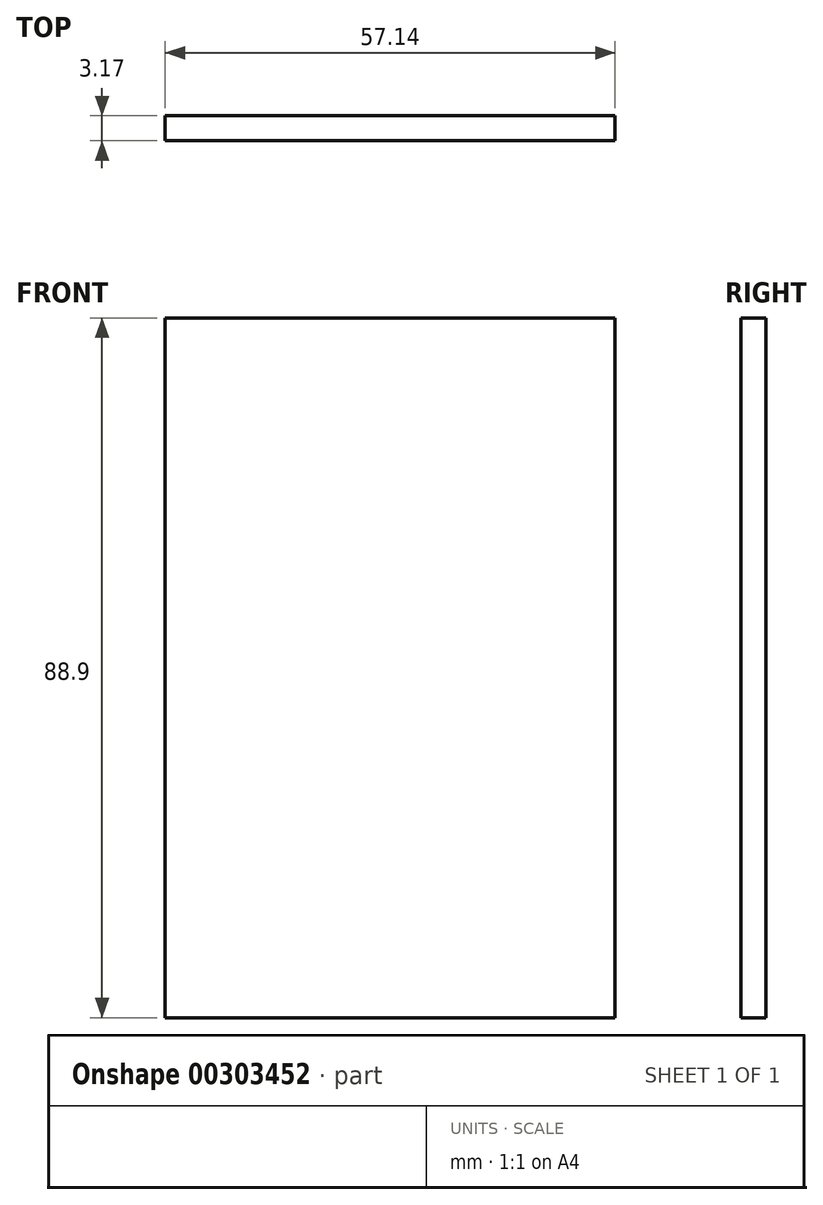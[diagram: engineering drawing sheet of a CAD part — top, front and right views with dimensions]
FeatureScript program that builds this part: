
annotation { "Feature Type Name" : "Feature", "Feature Type Description" : "" }
export const myFeature = defineFeature(function(context is Context, id is Id, definition is map)
    precondition{}
    {
        {
            var Q0;
            Q0=qCreatedBy(makeId("Front.planeOp"),FACE);
            var sketch = newSketch(context, id + "F0", { "sketchPlane" : qUnion([Q0])});
            skLineSegment(sketch, "E0.bottom", {"start": v(-28.58, 44.45) * mm, "end": v(28.57, 44.45) * mm});
            skLineSegment(sketch, "E0.top", {"start": v(-28.58, -44.45) * mm, "end": v(28.58, -44.45) * mm});
            skLineSegment(sketch, "E0.left", {"start": v(-28.58, 44.45) * mm, "end": v(-28.57, -44.45) * mm});
            skLineSegment(sketch, "E0.right", {"start": v(28.57, 44.45) * mm, "end": v(28.58, -44.45) * mm});
            skPoint(sketch, "E0.middle", {"position": v(0, 0) * mm});
            skSolve(sketch);
        }
        {
            var Q0;
            Q0 = qSketchRegion(id + "F0", true);
            extrude(context, id + "F1", {"entities" : qUnion([Q0]), "depth" : 3.17 * mm});
        }
    });
